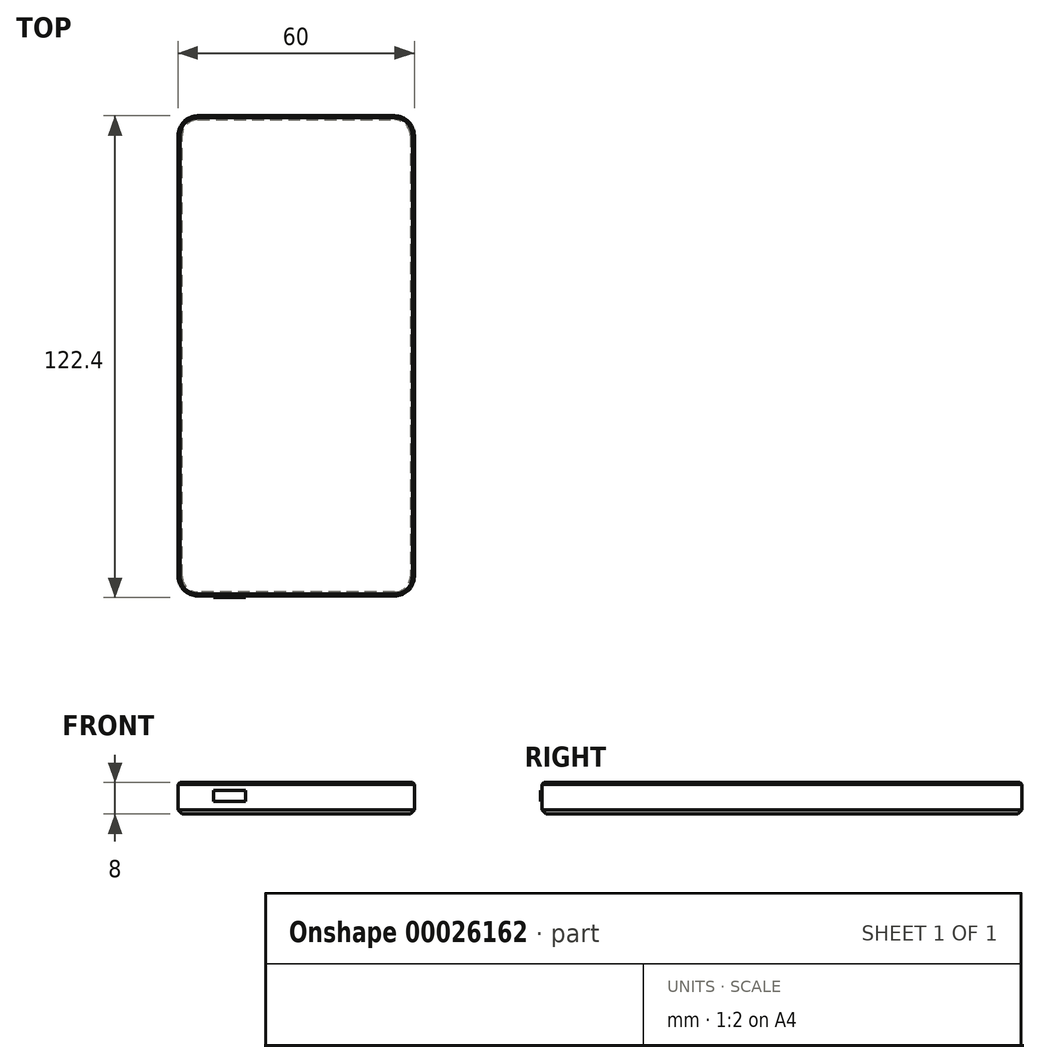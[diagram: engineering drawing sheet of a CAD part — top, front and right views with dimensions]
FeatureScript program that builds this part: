
annotation { "Feature Type Name" : "Feature", "Feature Type Description" : "" }
export const myFeature = defineFeature(function(context is Context, id is Id, definition is map)
    precondition{}
    {
        {
            var Q0;
            Q0=qCreatedBy(makeId("Top.planeOp"),FACE);
            var sketch = newSketch(context, id + "F0", { "sketchPlane" : qUnion([Q0])});
            skLineSegment(sketch, "E0.rect.bottom", {"start": v(30, 61) * mm, "end": v(-30, 61) * mm});
            skLineSegment(sketch, "E0.rect.top", {"start": v(30, -61) * mm, "end": v(-30, -61) * mm});
            skLineSegment(sketch, "E0.rect.left", {"start": v(30, 61) * mm, "end": v(30, -61) * mm});
            skLineSegment(sketch, "E0.rect.right", {"start": v(-30, 61) * mm, "end": v(-30, -61) * mm});
            skPoint(sketch, "E0.rect.middle", {"position": v(0, 0) * mm});
            skSolve(sketch);
        }
        {
            var Q0;
            Q0=makeQuery(id+"F0.imprint","IMPRINT",FACE,{"disambiguationData":[TD([[makeQuery(id+"F0.imprint","IMPRINT",EDGE,{"derivedFrom":sQuery(id+"F0.wireOp",EDGE,"E0.rect.bottom")}),1.0]])]});
            extrude(context, id + "F1", {"entities" : qUnion([Q0]), "depth" : 8 * mm});
        }
        {
            var Q0;
            Q0=makeQuery(id+"F1.opExtrude","SWEPT_EDGE",EDGE,{"disambiguationData":[OSD([sQuery(id+"F0.wireOp",EDGE,"E0.rect.top"),sQuery(id+"F0.wireOp",EDGE,"E0.rect.left")])]});
            var Q1;
            Q1=makeQuery(id+"F1.opExtrude","SWEPT_EDGE",EDGE,{"disambiguationData":[OSD([sQuery(id+"F0.wireOp",EDGE,"E0.rect.top"),sQuery(id+"F0.wireOp",EDGE,"E0.rect.right")])]});
            var Q2;
            Q2=makeQuery(id+"F1.opExtrude","SWEPT_EDGE",EDGE,{"disambiguationData":[OSD([sQuery(id+"F0.wireOp",EDGE,"E0.rect.bottom"),sQuery(id+"F0.wireOp",EDGE,"E0.rect.left")])]});
            var Q3;
            Q3=makeQuery(id+"F1.opExtrude","SWEPT_EDGE",EDGE,{"disambiguationData":[OSD([sQuery(id+"F0.wireOp",EDGE,"E0.rect.bottom"),sQuery(id+"F0.wireOp",EDGE,"E0.rect.right")])]});
            fillet(context, id + "F2", {"entities" : qUnion([Q0, Q1, Q2, Q3]), "radius" : 5 * mm, "tangentPropagation" : true, "allowEdgeOverflow" : false});
        }
        {
            var Q0;
            Q0=makeQuery(id+"F1.opExtrude","CAP_EDGE",EDGE,{"disambiguationData":[OSD([sQuery(id+"F0.wireOp",EDGE,"E0.rect.right")])],"isStart":false});
            var Q1;
            Q1=makeQuery(id+"F1.opExtrude","CAP_FACE",FACE,{"disambiguationData":[OSD([sQuery(id+"F0.wireOp",EDGE,"E0.rect.bottom"),sQuery(id+"F0.wireOp",EDGE,"E0.rect.top"),sQuery(id+"F0.wireOp",EDGE,"E0.rect.left"),sQuery(id+"F0.wireOp",EDGE,"E0.rect.right")])],"isStart":false});
            var Q2;
            Q2=makeQuery(id+"F1.opExtrude","CAP_EDGE",EDGE,{"disambiguationData":[OSD([sQuery(id+"F0.wireOp",EDGE,"E0.rect.left")])],"isStart":false});
            var Q3;
            Q3=makeQuery(id+"F1.opExtrude","CAP_EDGE",EDGE,{"disambiguationData":[OSD([sQuery(id+"F0.wireOp",EDGE,"E0.rect.top")])],"isStart":false});
            var Q4;
            Q4=makeQuery(id+"F1.opExtrude","CAP_EDGE",EDGE,{"disambiguationData":[OSD([sQuery(id+"F0.wireOp",EDGE,"E0.rect.bottom")])],"isStart":false});
            var Q5;
            {var subQ0=sQuery(id+"F0.wireOp",EDGE,"E0.rect.bottom");var subQ1=sQuery(id+"F0.wireOp",EDGE,"E0.rect.right");Q5=makeQuery(id+"F2.opFillet","BLEND_EDGE",EDGE,{"blendedFrom":[makeQuery(id+"F1.opExtrude","SWEPT_EDGE",EDGE,{"disambiguationData":[OSD([subQ0,subQ1])]}),makeQuery(id+"F1.opExtrude","CAP_FACE",FACE,{"disambiguationData":[OSD([subQ0,sQuery(id+"F0.wireOp",EDGE,"E0.rect.top"),sQuery(id+"F0.wireOp",EDGE,"E0.rect.left"),subQ1])],"isStart":false})],"blendedInto":[makeQuery(id+"F1.opExtrude","CAP_FACE",FACE,{"disambiguationData":[OSD([subQ0,sQuery(id+"F0.wireOp",EDGE,"E0.rect.top"),sQuery(id+"F0.wireOp",EDGE,"E0.rect.left"),subQ1])],"isStart":false})]});}
            var Q6;
            {var subQ0=sQuery(id+"F0.wireOp",EDGE,"E0.rect.bottom");var subQ1=sQuery(id+"F0.wireOp",EDGE,"E0.rect.left");Q6=makeQuery(id+"F2.opFillet","BLEND_EDGE",EDGE,{"blendedFrom":[makeQuery(id+"F1.opExtrude","SWEPT_EDGE",EDGE,{"disambiguationData":[OSD([subQ0,subQ1])]}),makeQuery(id+"F1.opExtrude","CAP_FACE",FACE,{"disambiguationData":[OSD([subQ0,sQuery(id+"F0.wireOp",EDGE,"E0.rect.top"),subQ1,sQuery(id+"F0.wireOp",EDGE,"E0.rect.right")])],"isStart":false})],"blendedInto":[makeQuery(id+"F1.opExtrude","CAP_FACE",FACE,{"disambiguationData":[OSD([subQ0,sQuery(id+"F0.wireOp",EDGE,"E0.rect.top"),subQ1,sQuery(id+"F0.wireOp",EDGE,"E0.rect.right")])],"isStart":false})]});}
            var Q7;
            {var subQ0=sQuery(id+"F0.wireOp",EDGE,"E0.rect.top");var subQ1=sQuery(id+"F0.wireOp",EDGE,"E0.rect.right");Q7=makeQuery(id+"F2.opFillet","BLEND_EDGE",EDGE,{"blendedFrom":[makeQuery(id+"F1.opExtrude","SWEPT_EDGE",EDGE,{"disambiguationData":[OSD([subQ0,subQ1])]}),makeQuery(id+"F1.opExtrude","CAP_FACE",FACE,{"disambiguationData":[OSD([sQuery(id+"F0.wireOp",EDGE,"E0.rect.bottom"),subQ0,sQuery(id+"F0.wireOp",EDGE,"E0.rect.left"),subQ1])],"isStart":false})],"blendedInto":[makeQuery(id+"F1.opExtrude","CAP_FACE",FACE,{"disambiguationData":[OSD([sQuery(id+"F0.wireOp",EDGE,"E0.rect.bottom"),subQ0,sQuery(id+"F0.wireOp",EDGE,"E0.rect.left"),subQ1])],"isStart":false})]});}
            var Q8;
            {var subQ0=sQuery(id+"F0.wireOp",EDGE,"E0.rect.top");var subQ1=sQuery(id+"F0.wireOp",EDGE,"E0.rect.left");Q8=makeQuery(id+"F2.opFillet","BLEND_EDGE",EDGE,{"blendedFrom":[makeQuery(id+"F1.opExtrude","SWEPT_EDGE",EDGE,{"disambiguationData":[OSD([subQ0,subQ1])]}),makeQuery(id+"F1.opExtrude","CAP_FACE",FACE,{"disambiguationData":[OSD([sQuery(id+"F0.wireOp",EDGE,"E0.rect.bottom"),subQ0,subQ1,sQuery(id+"F0.wireOp",EDGE,"E0.rect.right")])],"isStart":false})],"blendedInto":[makeQuery(id+"F1.opExtrude","CAP_FACE",FACE,{"disambiguationData":[OSD([sQuery(id+"F0.wireOp",EDGE,"E0.rect.bottom"),subQ0,subQ1,sQuery(id+"F0.wireOp",EDGE,"E0.rect.right")])],"isStart":false})]});}
            chamfer(context, id + "F3", {"entities" : qUnion([Q0, Q1, Q2, Q3, Q4, Q5, Q6, Q7, Q8]), "width" : .5 * mm, "tangentPropagation" : true});
        }
        {
            var Q0;
            Q0=makeQuery(id+"F1.opExtrude","CAP_EDGE",EDGE,{"disambiguationData":[OSD([sQuery(id+"F0.wireOp",EDGE,"E0.rect.right")])],"isStart":true});
            var Q1;
            Q1=makeQuery(id+"F1.opExtrude","CAP_EDGE",EDGE,{"disambiguationData":[OSD([sQuery(id+"F0.wireOp",EDGE,"E0.rect.top")])],"isStart":true});
            var Q2;
            {var subQ0=sQuery(id+"F0.wireOp",EDGE,"E0.rect.top");var subQ1=sQuery(id+"F0.wireOp",EDGE,"E0.rect.right");Q2=makeQuery(id+"F2.opFillet","BLEND_EDGE",EDGE,{"blendedFrom":[makeQuery(id+"F1.opExtrude","SWEPT_EDGE",EDGE,{"disambiguationData":[OSD([subQ0,subQ1])]}),makeQuery(id+"F1.opExtrude","CAP_FACE",FACE,{"disambiguationData":[OSD([sQuery(id+"F0.wireOp",EDGE,"E0.rect.bottom"),subQ0,sQuery(id+"F0.wireOp",EDGE,"E0.rect.left"),subQ1])],"isStart":true})],"blendedInto":[makeQuery(id+"F1.opExtrude","CAP_FACE",FACE,{"disambiguationData":[OSD([sQuery(id+"F0.wireOp",EDGE,"E0.rect.bottom"),subQ0,sQuery(id+"F0.wireOp",EDGE,"E0.rect.left"),subQ1])],"isStart":true})]});}
            var Q3;
            {var subQ0=sQuery(id+"F0.wireOp",EDGE,"E0.rect.top");var subQ1=sQuery(id+"F0.wireOp",EDGE,"E0.rect.left");Q3=makeQuery(id+"F2.opFillet","BLEND_EDGE",EDGE,{"blendedFrom":[makeQuery(id+"F1.opExtrude","SWEPT_EDGE",EDGE,{"disambiguationData":[OSD([subQ0,subQ1])]}),makeQuery(id+"F1.opExtrude","CAP_FACE",FACE,{"disambiguationData":[OSD([sQuery(id+"F0.wireOp",EDGE,"E0.rect.bottom"),subQ0,subQ1,sQuery(id+"F0.wireOp",EDGE,"E0.rect.right")])],"isStart":true})],"blendedInto":[makeQuery(id+"F1.opExtrude","CAP_FACE",FACE,{"disambiguationData":[OSD([sQuery(id+"F0.wireOp",EDGE,"E0.rect.bottom"),subQ0,subQ1,sQuery(id+"F0.wireOp",EDGE,"E0.rect.right")])],"isStart":true})]});}
            var Q4;
            Q4=makeQuery(id+"F1.opExtrude","CAP_EDGE",EDGE,{"disambiguationData":[OSD([sQuery(id+"F0.wireOp",EDGE,"E0.rect.left")])],"isStart":true});
            var Q5;
            {var subQ0=sQuery(id+"F0.wireOp",EDGE,"E0.rect.bottom");var subQ1=sQuery(id+"F0.wireOp",EDGE,"E0.rect.left");Q5=makeQuery(id+"F2.opFillet","BLEND_EDGE",EDGE,{"blendedFrom":[makeQuery(id+"F1.opExtrude","SWEPT_EDGE",EDGE,{"disambiguationData":[OSD([subQ0,subQ1])]}),makeQuery(id+"F1.opExtrude","CAP_FACE",FACE,{"disambiguationData":[OSD([subQ0,sQuery(id+"F0.wireOp",EDGE,"E0.rect.top"),subQ1,sQuery(id+"F0.wireOp",EDGE,"E0.rect.right")])],"isStart":true})],"blendedInto":[makeQuery(id+"F1.opExtrude","CAP_FACE",FACE,{"disambiguationData":[OSD([subQ0,sQuery(id+"F0.wireOp",EDGE,"E0.rect.top"),subQ1,sQuery(id+"F0.wireOp",EDGE,"E0.rect.right")])],"isStart":true})]});}
            var Q6;
            Q6=makeQuery(id+"F1.opExtrude","CAP_EDGE",EDGE,{"disambiguationData":[OSD([sQuery(id+"F0.wireOp",EDGE,"E0.rect.bottom")])],"isStart":true});
            var Q7;
            {var subQ0=sQuery(id+"F0.wireOp",EDGE,"E0.rect.bottom");var subQ1=sQuery(id+"F0.wireOp",EDGE,"E0.rect.right");Q7=makeQuery(id+"F2.opFillet","BLEND_EDGE",EDGE,{"blendedFrom":[makeQuery(id+"F1.opExtrude","SWEPT_EDGE",EDGE,{"disambiguationData":[OSD([subQ0,subQ1])]}),makeQuery(id+"F1.opExtrude","CAP_FACE",FACE,{"disambiguationData":[OSD([subQ0,sQuery(id+"F0.wireOp",EDGE,"E0.rect.top"),sQuery(id+"F0.wireOp",EDGE,"E0.rect.left"),subQ1])],"isStart":true})],"blendedInto":[makeQuery(id+"F1.opExtrude","CAP_FACE",FACE,{"disambiguationData":[OSD([subQ0,sQuery(id+"F0.wireOp",EDGE,"E0.rect.top"),sQuery(id+"F0.wireOp",EDGE,"E0.rect.left"),subQ1])],"isStart":true})]});}
            chamfer(context, id + "F4", {"entities" : qUnion([Q0, Q1, Q2, Q3, Q4, Q5, Q6, Q7]), "width" : 1 * mm, "tangentPropagation" : true});
        }
        {
            var Q0;
            Q0=makeQuery(id+"F1.opExtrude","SWEPT_FACE",FACE,{"disambiguationData":[OSD([sQuery(id+"F0.wireOp",EDGE,"E0.rect.top")])]});
            var sketch = newSketch(context, id + "F5", { "sketchPlane" : qUnion([Q0])});
            skLineSegment(sketch, "E1.rect.bottom", {"start": v(-21.06, 6.01) * mm, "end": v(-12.82, 6.01) * mm});
            skLineSegment(sketch, "E1.rect.top", {"start": v(-21.06, 3.16) * mm, "end": v(-12.82, 3.16) * mm});
            skLineSegment(sketch, "E1.rect.left", {"start": v(-21.06, 6.01) * mm, "end": v(-21.06, 3.16) * mm});
            skLineSegment(sketch, "E1.rect.right", {"start": v(-12.82, 6.01) * mm, "end": v(-12.82, 3.16) * mm});
            skPoint(sketch, "E1.rect.middle", {"position": v(-16.94, 4.59) * mm});
            skSolve(sketch);
        }
        {
            var Q0;
            Q0=makeQuery(id+"F5.imprint","IMPRINT",FACE,{"disambiguationData":[TD([[makeQuery(id+"F5.imprint","IMPRINT",EDGE,{"derivedFrom":sQuery(id+"F5.wireOp",EDGE,"E1.rect.bottom")}),-1.0]])]});
            extrude(context, id + "F6", {"entities" : qUnion([Q0]), "operationType" : NewBodyOperationType.ADD, "depth" : .4 * mm});
        }
    });
